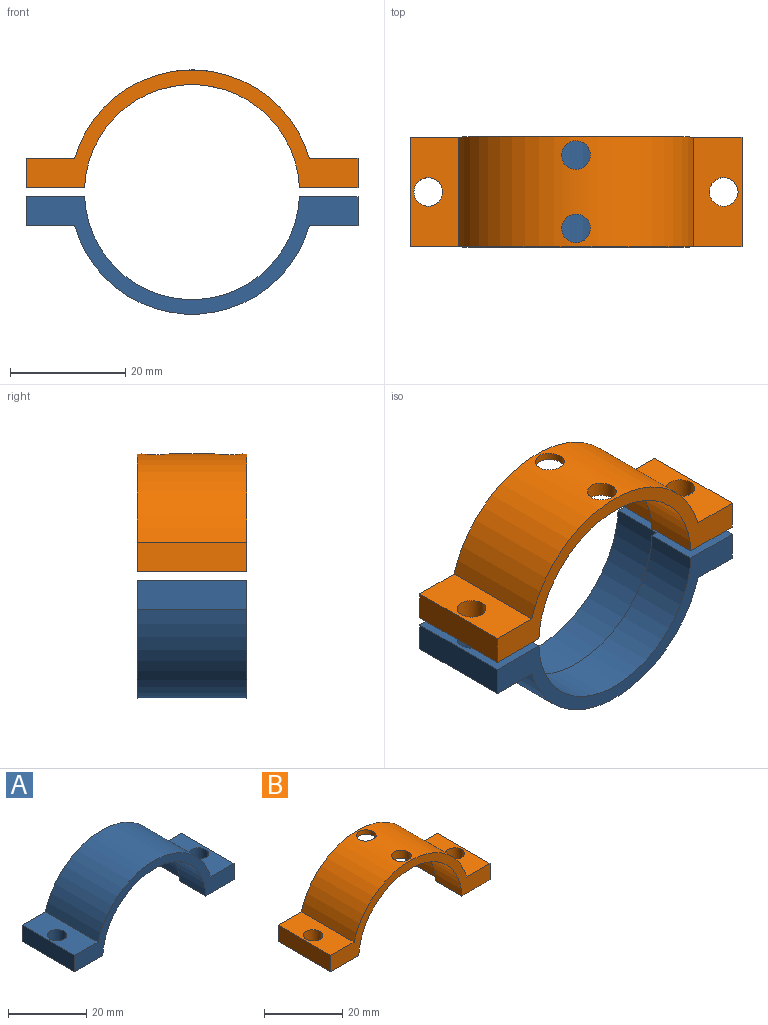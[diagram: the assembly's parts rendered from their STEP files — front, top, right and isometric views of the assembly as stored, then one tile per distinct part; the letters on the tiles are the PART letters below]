
ASSEMBLY  parts=2 mates=3
PART A: 14 faces, bbox 57.6x19.1x20.4 mm
  f0: cylinder r=18.64mm len=37.26mm, axis (0,1,0), area 543.4mm2, adj f1,f6,f8,f9
  f1: plane 19.05x10.16mm, normal (0,0,-1), area 162.3mm2, adj f0,f2,f3,f6,f7,f8,f13
  f2: plane 57.58x20.42mm, normal (0,1,0), area 162.8mm2, adj f1,f3,f4,f5,f7,f9,f10,f11
  f3: plane 19.05x5.08mm, normal (1,0,0), area 96.8mm2, adj f1,f2,f4,f6
  f4: plane 19.05x8.43mm, normal (0,0,1), area 141mm2, adj f2,f3,f5,f6,f13
  f5: cylinder r=21.18mm len=40.72mm, axis (0,1,0), area 1042.3mm2, adj f2,f4,f6,f11
  f6: plane 57.58x20.42mm, normal (0,-1,0), area 235.5mm2, adj f0,f1,f3,f4,f5,f9,f10,f11
  f7: cylinder r=19.88mm len=39.72mm, axis (0,1,0), area 580.2mm2, adj f1,f2,f8,f9
  f8: plane 39.72x19.11mm, normal (0,1,0), area 72.7mm2, adj f0,f1,f7,f9
  f9: plane 19.05x10.16mm, normal (0,0,-1), area 162.3mm2, adj f0,f2,f6,f7,f8,f10,f12
  f10: plane 19.05x5.08mm, normal (-1,0,0), area 96.8mm2, adj f2,f6,f9,f11
  f11: plane 19.05x8.43mm, normal (0,0,1), area 141mm2, adj f2,f5,f6,f10,f12
  f12: cylinder r=2.49mm len=5.08mm, axis (0,0,1), area 79.5mm2, adj f9,f11
  f13: cylinder r=2.49mm len=5.08mm, axis (0,0,1), area 79.5mm2, adj f1,f4
PART B: 16 faces, bbox 57.6x19.1x20.4 mm
  f0: cylinder r=18.64mm len=37.26mm, axis (0,1,0), area 523.9mm2, adj f3,f7,f8,f9,f14
  f1: cylinder r=21.18mm len=40.72mm, axis (0,1,0), area 1003.3mm2, adj f4,f6,f7,f11,f13,f14
  f2: cylinder r=19.88mm len=39.72mm, axis (0,1,0), area 560.7mm2, adj f3,f4,f8,f9,f13
  f3: plane 19.05x10.16mm, normal (0,0,-1), area 162.3mm2, adj f0,f2,f4,f5,f7,f8,f15
  f4: plane 57.58x20.42mm, normal (0,1,0), area 162.8mm2, adj f1,f2,f3,f5,f6,f9,f10,f11
  f5: plane 19.05x5.08mm, normal (1,0,0), area 96.8mm2, adj f3,f4,f6,f7
  f6: plane 19.05x8.43mm, normal (0,0,1), area 141mm2, adj f1,f4,f5,f7,f15
  f7: plane 57.58x20.42mm, normal (0,-1,0), area 235.5mm2, adj f0,f1,f3,f5,f6,f9,f10,f11
  f8: plane 39.72x19.11mm, normal (0,1,0), area 72.7mm2, adj f0,f2,f3,f9
  f9: plane 19.05x10.16mm, normal (0,0,-1), area 162.3mm2, adj f0,f2,f4,f7,f8,f10,f12
  f10: plane 19.05x5.08mm, normal (-1,0,0), area 96.8mm2, adj f4,f7,f9,f11
  f11: plane 19.05x8.43mm, normal (0,0,1), area 141mm2, adj f1,f4,f7,f10,f12
  f12: cylinder r=2.49mm len=5.08mm, axis (0,0,-1), area 79.5mm2, adj f9,f11
  f13: cylinder r=2.49mm len=4.98mm, axis (0,0,-1), area 20.5mm2, adj f1,f2
  f14: cylinder r=2.49mm len=4.98mm, axis (0,0,-1), area 39.9mm2, adj f0,f1
  f15: cylinder r=2.49mm len=5.08mm, axis (0,0,-1), area 79.5mm2, adj f3,f6
PLACE A rot(axis=(0,1,0),180deg) t=(-26.37,-37.14,-32.87)mm
PLACE B t=(-26.37,-37.14,-32.87)mm fixed
MATE parallel A.f9 <-> B.f3  axis (0,0,1) through (-2.57,-47.01,-33.63)mm
MATE planar A.f3 <-> B.f10  axis (-1,0,0) through (-55.16,-46.66,-36.17)mm
MATE planar A.f2 <-> B.f4  axis (0,1,0) through (2.42,-37.14,-36.17)mm
